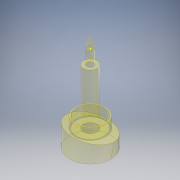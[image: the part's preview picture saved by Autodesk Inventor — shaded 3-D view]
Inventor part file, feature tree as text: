
AUTODESK INVENTOR PART (.ipt)
format: ipt  version: 2017 (Build 210142000, 142)  size: 159,232 bytes
history: native  units: mm
features: sketch x7, extrude x3, plane x2, loft x2, other x1
ambient origin geometry x8: Origin, YZ Plane, XZ Plane, XY Plane, X Axis, Y Axis, Z Axis, Center Point
bodies: Body1 (feature_tree)
feature tree (15):
  sketch  "Sketch1"  dims[d0=15.0mm d7=0.0mm d8=90.0deg]
  plane  "Work Plane1"
  loft  "Loft1"
  extrude  "Extrusion2"  Depth=10.0mm
  extrude  "Extrusion3"  Depth=4.0mm TaperAngle=0.0deg
  extrude  "Extrusion4"  Depth=20.0mm TaperAngle=0.0deg
  sketch  "Sketch6"  dims[d21=5.0mm]
  plane  "Work Plane2"
  loft  "Loft2"
  sketch  "Sketch2"  dims[d9=0.0mm d10=90.0deg d11=10.0mm]
  sketch  "Sketch3"  dims[d12=11.0mm d13=4.0mm d14=0.0mm]
  sketch  "Sketch4"  dims[d15=5.0mm d16=20.0mm d17=0.0mm]
  sketch  "Sketch5"  dims[d18=2.5mm d19=5.0mm d20=0.0mm]
  sketch  "Sketch7"  dims[d22=0.0mm d23=90.0deg d24=0.0mm d25=90.0deg d26=7.5mm]
  other  "Edges1"
